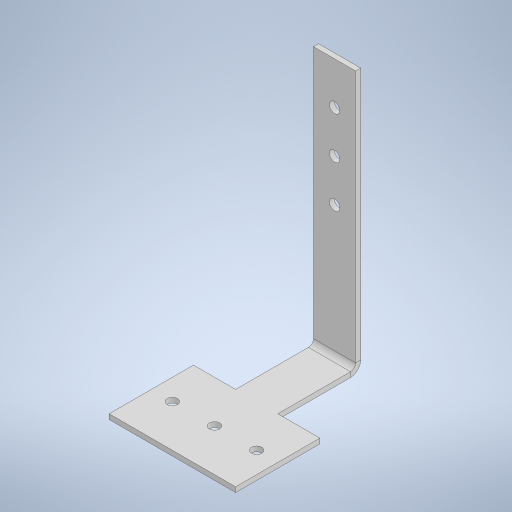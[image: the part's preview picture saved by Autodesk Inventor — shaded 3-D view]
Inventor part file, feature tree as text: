
AUTODESK INVENTOR PART (.ipt)
format: ipt  version: 2023 (Build 270158000, 158)  size: 1,115,648 bytes
history: native  units: in
note: dims shown in document units (in); Inventor stores cm internally (conversion verified against a paired STEP export)
features: sketch x3, sheet_metal_op x2, hole x1, other x1
ambient origin geometry x8: Origin, YZ Plane, XZ Plane, XY Plane, X Axis, Y Axis, Z Axis, Center Point
bodies: Body1 (feature_tree)
feature tree (7):
  sheet_metal_op  "Face3"
  hole  "Hole1"  [1 undecoded]
  sheet_metal_op  "Fold3"
  sketch  "Sketch7"  dims[d17=1.0in d18=10.0in]
  other  "Plate3"
  sketch  "Sketch8"  dims[d19=1.0in]
  sketch  "Sketch9"  dims[d20=0.12in d21=1.0in d22=2.0in d23=3.0in d24=0.25in d25=0.75in d26=0.375in d27=0.25in d28=0.5635in d29=0.12in d30=0.8108in d31=3.0in d32=0.12in d33=0.06in d34=0.24in d35=0.12in d36=90.0deg d37=0.12in d38=3.0in d39=2.0in d40=1.0in d41=1.0in]
note: 1 required parameter value undecoded (feature->parameter linkage not recoverable at this tier; creation-order binding heuristic only, values carry confidence <= 0.55)
